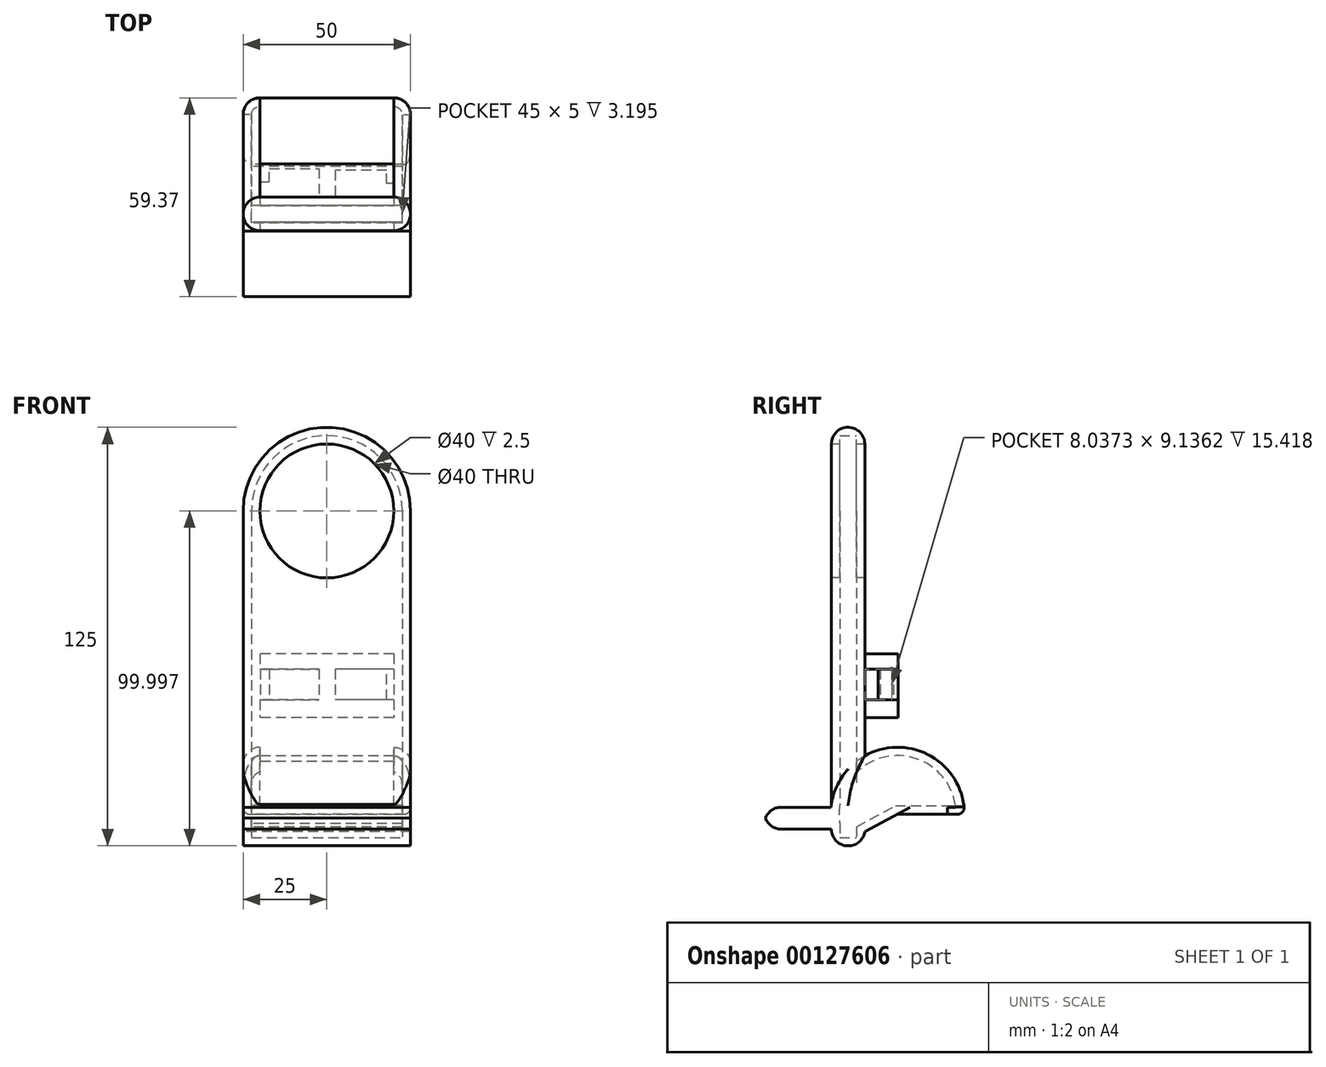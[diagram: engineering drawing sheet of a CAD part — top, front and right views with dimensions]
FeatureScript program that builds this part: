
annotation { "Feature Type Name" : "Feature", "Feature Type Description" : "" }
export const myFeature = defineFeature(function(context is Context, id is Id, definition is map)
    precondition{}
    {
        {
            var Q0;
            Q0=qCreatedBy(makeId("Front.planeOp"),FACE);
            var sketch = newSketch(context, id + "F0", { "sketchPlane" : qUnion([Q0])});
            skArc(sketch, "E0", {"start": v(25, 25.3) * mm, "mid": v(0, 50.3) * mm, "end": v(-25, 25.3) * mm});
            skLineSegment(sketch, "E1.bottom", {"start": v(-25, 25.3) * mm, "end": v(25, 25.3) * mm});
            skLineSegment(sketch, "E1.top", {"start": v(-25, -74.7) * mm, "end": v(25, -74.7) * mm});
            skLineSegment(sketch, "E1.left", {"start": v(-25, 25.3) * mm, "end": v(-25, -74.7) * mm});
            skLineSegment(sketch, "E1.right", {"start": v(25, 25.3) * mm, "end": v(25, -74.7) * mm});
            skSolve(sketch);
        }
        {
            var Q0;
            Q0 = qSketchRegion(id + "F0", true);
            extrude(context, id + "F1", {"entities" : qUnion([Q0]), "depth" : 10 * mm});
        }
        {
            var Q0;
            Q0=makeQuery(id+"F1.opExtrude","SWEPT_FACE",FACE,{"disambiguationData":[OSD([sQuery(id+"F0.wireOp",EDGE,"E1.left")])]});
            var sketch = newSketch(context, id + "F2", { "sketchPlane" : qUnion([Q0])});
            skArc(sketch, "E2", {"start": v(7.85, -74.7) * mm, "mid": v(-4.93, -45.86) * mm, "end": v(-29.79, -65.26) * mm});
            skLineSegment(sketch, "E3", {"start": v(7.85, -74.7) * mm, "end": v(-9.79, -65.26) * mm});
            skLineSegment(sketch, "E4", {"start": v(-9.79, -65.26) * mm, "end": v(-29.79, -65.26) * mm});
            skSolve(sketch);
        }
        {
            var Q0;
            Q0 = qSketchRegion(id + "F2", true);
            extrude(context, id + "F3", {"entities" : qUnion([Q0]), "operationType" : NewBodyOperationType.ADD, "oppositeDirection" : true, "depth" : 50 * mm});
        }
        {
            var Q0;
            {var subQ1=sQuery(id+"F2.wireOp",EDGE,"E4");var subQ2=sQuery(id+"F2.wireOp",EDGE,"E2");Q0=makeQuery(id+"F3.boolean.opBoolean","SPLIT",EDGE,{"disambiguationData":[TD([makeQuery(id+"F3.opExtrude","SWEPT_FACE",FACE,{"disambiguationData":[OSD([subQ1])]})])],"derivedFrom":makeQuery(id+"F3.opExtrude","CAP_EDGE",EDGE,{"disambiguationData":[OSD([subQ2])],"isStart":true})});}
            var Q1;
            {var subQ1=sQuery(id+"F2.wireOp",EDGE,"E2");var subQ2=sQuery(id+"F2.wireOp",EDGE,"E4");Q1=makeQuery(id+"F3.boolean.opBoolean","SPLIT",EDGE,{"disambiguationData":[TD([makeQuery(id+"F3.opExtrude","SWEPT_FACE",FACE,{"disambiguationData":[OSD([subQ2])]})])],"derivedFrom":makeQuery(id+"F3.opExtrude","CAP_EDGE",EDGE,{"disambiguationData":[OSD([subQ1])],"isStart":false})});}
            fillet(context, id + "F4", {"entities" : qUnion([Q0, Q1]), "radius" : 5 * mm, "tangentPropagation" : true, "allowEdgeOverflow" : false});
        }
        {
            var Q0;
            {var subQ2=sQuery(id+"F2.wireOp",EDGE,"E4");var subQ4=sQuery(id+"F2.wireOp",EDGE,"E2");Q0=makeQuery(id+"F3.boolean.opBoolean","SPLIT",FACE,{"disambiguationData":[TD([makeQuery(id+"F3.opExtrude","SWEPT_FACE",FACE,{"disambiguationData":[OSD([subQ2])]})])],"derivedFrom":makeQuery(id+"F3.opExtrude","SWEPT_FACE",FACE,{"disambiguationData":[OSD([subQ4])]})});}
            shell(context, id + "F5", {"entities" : qUnion([Q0]), "thickness" : 2.5 * mm});
        }
        {
            var Q0;
            {var subQ0=sQuery(id+"F0.wireOp",EDGE,"E1.right");var subQ2=sQuery(id+"F0.wireOp",EDGE,"E1.left");var subQ5=sQuery(id+"F0.wireOp",EDGE,"E0");Q0=makeQuery(id+"F3.boolean.opBoolean","SPLIT",FACE,{"disambiguationData":[TD([makeQuery(id+"F1.opExtrude","SWEPT_FACE",FACE,{"disambiguationData":[OSD([subQ5])]})])],"derivedFrom":makeQuery(id+"F1.opExtrude","CAP_FACE",FACE,{"disambiguationData":[OSD([subQ5,sQuery(id+"F0.wireOp",EDGE,"E1.top"),subQ2,subQ0])],"isStart":false})});}
            var sketch = newSketch(context, id + "F6", { "sketchPlane" : qUnion([Q0])});
            skArc(sketch, "E5", {"start": v(19.98, 25.3) * mm, "mid": v(0, 45.29) * mm, "end": v(-19.98, 25.3) * mm});
            skLineSegment(sketch, "E6", {"start": v(-19.98, 25.3) * mm, "end": v(19.98, 25.3) * mm});
            skSolve(sketch);
        }
        {
            var Q0;
            Q0=sQuery(id+"F6.wireOp",VERTEX,"E5.center");
            var Q1;
            Q1=makeQuery(id+"F1.opExtrude","SWEPT_BODY",BODY,{"disambiguationData":[OSD([sQuery(id+"F0.wireOp",EDGE,"E0"),sQuery(id+"F0.wireOp",EDGE,"E1.top"),sQuery(id+"F0.wireOp",EDGE,"E1.left"),sQuery(id+"F0.wireOp",EDGE,"E1.right")])]});
            hole(context, id + "F7", {"style" : HoleStyle.SIMPLE, "endStyle" : HoleEndStyle.THROUGH, "holeDiameter" : 40 * mm, "locations" : qUnion([Q0]), "scope" : qUnion([Q1]), "isTappedThrough" : true});
        }
        {
            var Q0;
            Q0=makeQuery(id+"F1.opExtrude","CAP_EDGE",EDGE,{"disambiguationData":[OSD([sQuery(id+"F0.wireOp",EDGE,"E1.top")])],"isStart":false});
            fillet(context, id + "F8", {"entities" : qUnion([Q0]), "radius" : 5 * mm, "tangentPropagation" : true, "allowEdgeOverflow" : false});
        }
        {
            var Q0;
            Q0=makeQuery(id+"F1.opExtrude","CAP_EDGE",EDGE,{"disambiguationData":[OSD([sQuery(id+"F0.wireOp",EDGE,"E1.top")])],"isStart":true});
            fillet(context, id + "F9", {"entities" : qUnion([Q0]), "radius" : 5 * mm, "tangentPropagation" : true, "allowEdgeOverflow" : false});
        }
        {
            var Q0;
            {var subQ1=sQuery(id+"F0.wireOp",EDGE,"E1.right");var subQ2=sQuery(id+"F0.wireOp",EDGE,"E1.left");var subQ5=sQuery(id+"F0.wireOp",EDGE,"E1.top");Q0=makeQuery(id+"F3.boolean.opBoolean","SPLIT",FACE,{"disambiguationData":[TD([makeQuery(id+"F1.opExtrude","SWEPT_FACE",FACE,{"disambiguationData":[OSD([subQ5])]})])],"derivedFrom":makeQuery(id+"F1.opExtrude","CAP_FACE",FACE,{"disambiguationData":[OSD([sQuery(id+"F0.wireOp",EDGE,"E0"),subQ5,subQ2,subQ1])],"isStart":false})});}
            extrude(context, id + "F10", {"entities" : qUnion([Q0]), "operationType" : NewBodyOperationType.ADD, "depth" : 20 * mm});
        }
        {
            var Q0;
            Q0=makeQuery(id+"F10.opExtrude","SWEPT_FACE",FACE,{"disambiguationData":[OSD([sQuery(id+"F0.wireOp",EDGE,"E0"),sQuery(id+"F0.wireOp",EDGE,"E1.top"),sQuery(id+"F0.wireOp",EDGE,"E1.left"),sQuery(id+"F0.wireOp",EDGE,"E1.right"),sQuery(id+"F2.wireOp",EDGE,"E2")])]});
            extrude(context, id + "F11", {"entities" : qUnion([Q0]), "operationType" : NewBodyOperationType.ADD, "depth" : 5 * mm});
        }
        {
            var Q0;
            Q0=makeQuery(id+"F10.opExtrude","CAP_EDGE",EDGE,{"disambiguationData":[OSD([sQuery(id+"F0.wireOp",EDGE,"E0"),sQuery(id+"F0.wireOp",EDGE,"E1.top"),sQuery(id+"F0.wireOp",EDGE,"E1.left"),sQuery(id+"F0.wireOp",EDGE,"E1.right")])],"isStart":false});
            var Q1;
            {var subQ0=sQuery(id+"F2.wireOp",EDGE,"E2");var subQ1=sQuery(id+"F0.wireOp",EDGE,"E1.right");var subQ2=sQuery(id+"F0.wireOp",EDGE,"E1.left");var subQ3=sQuery(id+"F0.wireOp",EDGE,"E1.top");var subQ4=sQuery(id+"F0.wireOp",EDGE,"E0");Q1=makeQuery(id+"F11.opExtrude","CAP_EDGE",EDGE,{"disambiguationData":[OSD([subQ4,subQ3,subQ2,subQ1,subQ0]),TDD([makeQuery(id+"F10.opExtrude","CAP_EDGE",EDGE,{"disambiguationData":[OSD([subQ4,subQ3,subQ2,subQ1,subQ0])],"isStart":false})])],"isStart":false});}
            fillet(context, id + "F12", {"entities" : qUnion([Q0, Q1]), "radius" : 5 * mm, "tangentPropagation" : true, "allowEdgeOverflow" : false});
        }
        {
            var Q0;
            Q0=makeQuery(id+"F1.opExtrude","CAP_EDGE",EDGE,{"disambiguationData":[OSD([sQuery(id+"F0.wireOp",EDGE,"E0")])],"isStart":false});
            var Q1;
            Q1=makeQuery(id+"F1.opExtrude","CAP_EDGE",EDGE,{"disambiguationData":[OSD([sQuery(id+"F0.wireOp",EDGE,"E0")])],"isStart":true});
            fillet(context, id + "F13", {"entities" : qUnion([Q0, Q1]), "radius" : 5 * mm, "tangentPropagation" : true, "allowEdgeOverflow" : false});
        }
        {
            var Q0;
            Q0=makeQuery(id+"F3.opExtrude","SWEPT_EDGE",EDGE,{"disambiguationData":[OSD([sQuery(id+"F2.wireOp",EDGE,"E2"),sQuery(id+"F2.wireOp",EDGE,"E4")])]});
            fillet(context, id + "F14", {"entities" : qUnion([Q0]), "radius" : 2 * mm, "tangentPropagation" : true, "allowEdgeOverflow" : false});
        }
        {
            var Q0;
            {var subQ0=sQuery(id+"F0.wireOp",EDGE,"E1.right");var subQ2=sQuery(id+"F0.wireOp",EDGE,"E1.left");var subQ5=sQuery(id+"F0.wireOp",EDGE,"E0");Q0=makeQuery(id+"F3.boolean.opBoolean","SPLIT",FACE,{"disambiguationData":[TD([makeQuery(id+"F1.opExtrude","SWEPT_FACE",FACE,{"disambiguationData":[OSD([subQ5])]})])],"derivedFrom":makeQuery(id+"F1.opExtrude","CAP_FACE",FACE,{"disambiguationData":[OSD([subQ5,sQuery(id+"F0.wireOp",EDGE,"E1.top"),subQ2,subQ0])],"isStart":true})});}
            var sketch = newSketch(context, id + "F15", { "sketchPlane" : qUnion([Q0])});
            skLineSegment(sketch, "E7.bottom", {"start": v(-20, -17.38) * mm, "end": v(20, -17.38) * mm});
            skLineSegment(sketch, "E7.top", {"start": v(-20, -21.95) * mm, "end": v(20, -21.95) * mm});
            skLineSegment(sketch, "E7.left", {"start": v(-20, -17.38) * mm, "end": v(-20, -21.95) * mm});
            skLineSegment(sketch, "E7.right", {"start": v(20, -17.38) * mm, "end": v(20, -21.95) * mm});
            skLineSegment(sketch, "E8.bottom", {"start": v(-20, -31.08) * mm, "end": v(20, -31.08) * mm});
            skLineSegment(sketch, "E8.top", {"start": v(-20, -36.45) * mm, "end": v(20, -36.45) * mm});
            skLineSegment(sketch, "E8.left", {"start": v(-20, -31.08) * mm, "end": v(-20, -36.45) * mm});
            skLineSegment(sketch, "E8.right", {"start": v(20, -31.08) * mm, "end": v(20, -36.45) * mm});
            skSolve(sketch);
        }
        {
            var Q0;
            Q0 = qSketchRegion(id + "F15", true);
            extrude(context, id + "F16", {"entities" : qUnion([Q0]), "operationType" : NewBodyOperationType.ADD, "depth" : 10 * mm});
        }
        {
            var Q0;
            {var subQ0=sQuery(id+"F0.wireOp",EDGE,"E1.right");var subQ1=sQuery(id+"F0.wireOp",EDGE,"E1.left");var subQ5=sQuery(id+"F0.wireOp",EDGE,"E0");Q0=makeQuery(id+"F16.boolean.opBoolean","SPLIT",FACE,{"disambiguationData":[TD([makeQuery(id+"F16.opExtrude","SWEPT_FACE",FACE,{"disambiguationData":[OSD([sQuery(id+"F15.wireOp",EDGE,"E7.top")])]})])],"derivedFrom":makeQuery(id+"F3.boolean.opBoolean","SPLIT",FACE,{"disambiguationData":[TD([makeQuery(id+"F1.opExtrude","SWEPT_FACE",FACE,{"disambiguationData":[OSD([subQ5])]})])],"derivedFrom":makeQuery(id+"F1.opExtrude","CAP_FACE",FACE,{"disambiguationData":[OSD([subQ5,sQuery(id+"F0.wireOp",EDGE,"E1.top"),subQ1,subQ0])],"isStart":true})})});}
            var sketch = newSketch(context, id + "F17", { "sketchPlane" : qUnion([Q0])});
            skLineSegment(sketch, "E9.bottom", {"start": v(-2.48, -21.95) * mm, "end": v(2.37, -21.95) * mm});
            skLineSegment(sketch, "E9.top", {"start": v(-2.48, -31.08) * mm, "end": v(2.37, -31.08) * mm});
            skLineSegment(sketch, "E9.left", {"start": v(-2.48, -21.95) * mm, "end": v(-2.48, -31.08) * mm});
            skLineSegment(sketch, "E9.right", {"start": v(2.37, -21.95) * mm, "end": v(2.37, -31.08) * mm});
            skSolve(sketch);
        }
        {
            var Q0;
            Q0 = qSketchRegion(id + "F17", true);
            extrude(context, id + "F18", {"entities" : qUnion([Q0]), "operationType" : NewBodyOperationType.ADD, "depth" : 10 * mm});
        }
        {
            var Q0;
            Q0=makeQuery(id+"F18.opExtrude","SWEPT_FACE",FACE,{"disambiguationData":[OSD([sQuery(id+"F17.wireOp",EDGE,"E9.left")])]});
            var sketch = newSketch(context, id + "F19", { "sketchPlane" : qUnion([Q0])});
            skLineSegment(sketch, "E10.bottom", {"start": v(10, -21.95) * mm, "end": v(8.04, -21.95) * mm});
            skLineSegment(sketch, "E10.top", {"start": v(10, -31.08) * mm, "end": v(8.04, -31.08) * mm});
            skLineSegment(sketch, "E10.left", {"start": v(10, -21.95) * mm, "end": v(10, -31.08) * mm});
            skLineSegment(sketch, "E10.right", {"start": v(8.04, -21.95) * mm, "end": v(8.04, -31.08) * mm});
            skSolve(sketch);
        }
        {
            var Q0;
            Q0 = qSketchRegion(id + "F19", true);
            extrude(context, id + "F20", {"entities" : qUnion([Q0]), "operationType" : NewBodyOperationType.ADD, "depth" : 17.5 * mm});
        }
        {
            var Q0;
            Q0=makeQuery(id+"F18.opExtrude","SWEPT_FACE",FACE,{"disambiguationData":[OSD([sQuery(id+"F17.wireOp",EDGE,"E9.right")])]});
            var sketch = newSketch(context, id + "F21", { "sketchPlane" : qUnion([Q0])});
            skLineSegment(sketch, "E11.bottom", {"start": v(-10, -21.95) * mm, "end": v(-8.59, -21.95) * mm});
            skLineSegment(sketch, "E11.top", {"start": v(-10, -31.08) * mm, "end": v(-8.59, -31.08) * mm});
            skLineSegment(sketch, "E11.left", {"start": v(-10, -21.95) * mm, "end": v(-10, -31.08) * mm});
            skLineSegment(sketch, "E11.right", {"start": v(-8.59, -21.95) * mm, "end": v(-8.59, -31.08) * mm});
            skSolve(sketch);
        }
        {
            var Q0;
            Q0 = qSketchRegion(id + "F21", true);
            extrude(context, id + "F22", {"entities" : qUnion([Q0]), "operationType" : NewBodyOperationType.ADD, "depth" : 17.5 * mm});
        }
        {
            var Q0;
            Q0=makeQuery(id+"F22.opExtrude","SWEPT_FACE",FACE,{"disambiguationData":[OSD([sQuery(id+"F21.wireOp",EDGE,"E11.right")])]});
            var sketch = newSketch(context, id + "F23", { "sketchPlane" : qUnion([Q0])});
            skLineSegment(sketch, "E12.bottom", {"start": v(-19.87, -21.95) * mm, "end": v(-17.15, -21.95) * mm});
            skLineSegment(sketch, "E12.top", {"start": v(-19.87, -31.08) * mm, "end": v(-17.15, -31.08) * mm});
            skLineSegment(sketch, "E12.left", {"start": v(-19.87, -21.95) * mm, "end": v(-19.87, -31.08) * mm});
            skLineSegment(sketch, "E12.right", {"start": v(-17.15, -21.95) * mm, "end": v(-17.15, -31.08) * mm});
            skSolve(sketch);
        }
        {
            var Q0;
            Q0 = qSketchRegion(id + "F23", true);
            extrude(context, id + "F24", {"entities" : qUnion([Q0]), "operationType" : NewBodyOperationType.ADD, "depth" : 4 * mm});
        }
        {
            var Q0;
            Q0=makeQuery(id+"F20.opExtrude","SWEPT_FACE",FACE,{"disambiguationData":[OSD([sQuery(id+"F19.wireOp",EDGE,"E10.right")])]});
            var sketch = newSketch(context, id + "F25", { "sketchPlane" : qUnion([Q0])});
            skLineSegment(sketch, "E13.bottom", {"start": v(19.98, -31.08) * mm, "end": v(17.9, -31.08) * mm});
            skLineSegment(sketch, "E13.top", {"start": v(19.98, -21.95) * mm, "end": v(17.9, -21.95) * mm});
            skLineSegment(sketch, "E13.left", {"start": v(19.98, -31.08) * mm, "end": v(19.98, -21.95) * mm});
            skLineSegment(sketch, "E13.right", {"start": v(17.9, -31.08) * mm, "end": v(17.9, -21.95) * mm});
            skSolve(sketch);
        }
        {
            var Q0;
            Q0 = qSketchRegion(id + "F25", true);
            extrude(context, id + "F26", {"entities" : qUnion([Q0]), "operationType" : NewBodyOperationType.ADD, "depth" : 4 * mm});
        }
    });
